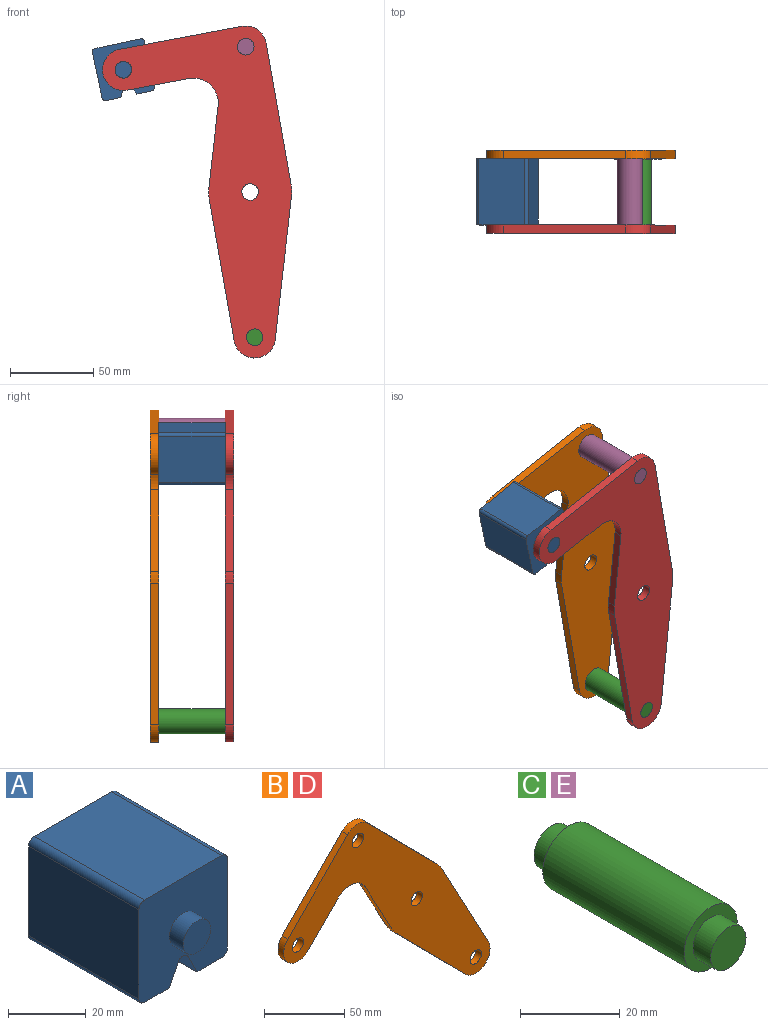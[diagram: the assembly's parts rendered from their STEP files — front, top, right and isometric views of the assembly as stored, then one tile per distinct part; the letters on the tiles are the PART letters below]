
ASSEMBLY  parts=5 mates=3
PART A: 18 faces, bbox 32.1x50x32.1 mm
  f0: plane 40x28.08mm, normal (1,0,0), area 1123.1mm2, adj f4,f10,f13,f14
  f1: plane 40x9.04mm, normal (0,0,-1), area 361.6mm2, adj f2,f4,f10,f14
  f2: plane 40x6.42mm, normal (-0.89,0,-0.45), area 287.2mm2, adj f1,f4,f10,f15
  f3: plane 40x6.42mm, normal (0.89,0,-0.45), area 287.2mm2, adj f4,f5,f10,f15
  f4: plane 32.08x32.08mm, normal (0,-1,0), area 900.6mm2, adj f0,f1,f2,f3,f5,f6,f7,f9
  f5: plane 40x9.04mm, normal (0,0,-1), area 361.6mm2, adj f3,f4,f10,f16
  f6: plane 40x28.08mm, normal (0,0,1), area 1123.1mm2, adj f4,f10,f13,f17
  f7: plane 40x28.08mm, normal (-1,0,0), area 1123.1mm2, adj f4,f10,f16,f17
  f8: plane 10x10mm, normal (0,-1,0), area 78.5mm2, adj f9
  f9: cylinder r=5mm len=10mm, axis (0,1,0), area 157.1mm2, adj f4,f8
  f10: plane 32.08x32.08mm, normal (0,1,0), area 900.6mm2, adj f0,f1,f2,f3,f5,f6,f7,f12
  f11: plane 10x10mm, normal (0,1,0), area 78.5mm2, adj f12
  f12: cylinder r=5mm len=10mm, axis (0,-1,0), area 157.1mm2, adj f10,f11
  f13: cylinder r=2mm len=40mm, axis (0,1,0), area 125.7mm2, adj f0,f4,f6,f10
  f14: cylinder r=2mm len=40mm, axis (0,-1,0), area 125.7mm2, adj f0,f1,f4,f10
  f15: cylinder r=2mm len=40mm, axis (0,1,0), area 177.1mm2, adj f2,f3,f4,f10
  f16: cylinder r=2mm len=40mm, axis (0,1,0), area 125.7mm2, adj f4,f5,f7,f10
  f17: cylinder r=2mm len=40mm, axis (0,-1,0), area 125.7mm2, adj f4,f6,f7,f10
PART B: 18 faces, bbox 181.7x5x165.8 mm
  f0: plane 43.49x23.35mm, normal (-0.88,0,-0.47), area 246.8mm2, adj f1,f14,f16,f17
  f1: cylinder r=25mm len=5.75mm, axis (0,1,0), area 35.8mm2, adj f0,f2,f16,f17
  f2: plane 61.6x60.87mm, normal (-0.71,0,-0.7), area 433mm2, adj f1,f3,f16,f17
  f3: cylinder r=12.5mm len=21.39mm, axis (0,1,0), area 178.4mm2, adj f2,f4,f16,f17
  f4: plane 76.3x40.96mm, normal (0.88,0,0.47), area 433mm2, adj f3,f5,f16,f17
  f5: cylinder r=25mm len=5.75mm, axis (0,1,0), area 35.8mm2, adj f4,f6,f16,f17
  f6: plane 61.6x60.87mm, normal (0.71,0,0.7), area 433mm2, adj f5,f7,f16,f17
  f7: cylinder r=12.5mm len=17.78mm, axis (0,1,0), area 98.9mm2, adj f6,f8,f16,f17
  f8: plane 53.35x52.71mm, normal (-0.71,0,0.7), area 375mm2, adj f7,f9,f16,f17
  f9: cylinder r=12.5mm len=21.39mm, axis (0,1,0), area 196.3mm2, adj f8,f10,f16,f17
  f10: plane 26.86x26.54mm, normal (0.71,0,-0.7), area 188.8mm2, adj f9,f14,f16,f17
  f11: cylinder r=5mm len=10mm, axis (0,1,0), area 157.1mm2, adj f16,f17
  f12: cylinder r=5mm len=10mm, axis (0,1,0), area 157.1mm2, adj f16,f17
  f13: cylinder r=5mm len=10mm, axis (0,1,0), area 157.1mm2, adj f16,f17
  f14: cylinder r=15mm len=23.89mm, axis (0,1,0), area 140.2mm2, adj f0,f10,f16,f17
  f15: cylinder r=5mm len=10mm, axis (0,1,0), area 157.1mm2, adj f16,f17
  f16: plane 181.66x165.78mm, normal (0,-1,0), area 8710.1mm2, adj f0,f1,f2,f3,f4,f5,f6,f7
  f17: plane 181.66x165.78mm, normal (0,1,0), area 8710.1mm2, adj f0,f1,f2,f3,f4,f5,f6,f7
PART C: 7 faces, bbox 15x50x15 mm
  f0: cylinder r=7.5mm len=40mm, axis (0,-1,0), area 1885mm2, adj f2,f5
  f1: cylinder r=5mm len=10mm, axis (0,1,0), area 157.1mm2, adj f2,f3
  f2: plane 15x15mm, normal (0,-1,0), area 98.2mm2, adj f0,f1
  f3: plane 10x10mm, normal (0,-1,0), area 78.5mm2, adj f1
  f4: cylinder r=5mm len=10mm, axis (0,-1,0), area 157.1mm2, adj f5,f6
  f5: plane 15x15mm, normal (0,1,0), area 98.2mm2, adj f0,f4
  f6: plane 10x10mm, normal (0,1,0), area 78.5mm2, adj f4
PART D: same geometry as B
PART E: same geometry as C
PLACE A rot(axis=(0,-1,0),12deg) t=(29.56,-20,78.77)mm
PLACE B rot(axis=(0,1,0),34.7deg) t=(0,25,0)mm
PLACE C rot(axis=(0,1,0),34.7deg) t=(5.34,-20,-174.92)mm
PLACE D rot(axis=(0,1,0),34.7deg) t=(0,-20,0)mm fixed
PLACE E rot(axis=(0,1,0),34.7deg) t=(0,-20,0)mm
MATE fastened D.f3 <-> C.f0  axis (0,1,0) through (2.67,-20,-87.46)mm
MATE revolute A.f9 <-> D.f9  axis (0,-1,0) through (-76.38,-20,73.6)mm
MATE fastened B.f7 <-> E.f0  axis (0,-1,0) through (-2.67,20,87.46)mm
